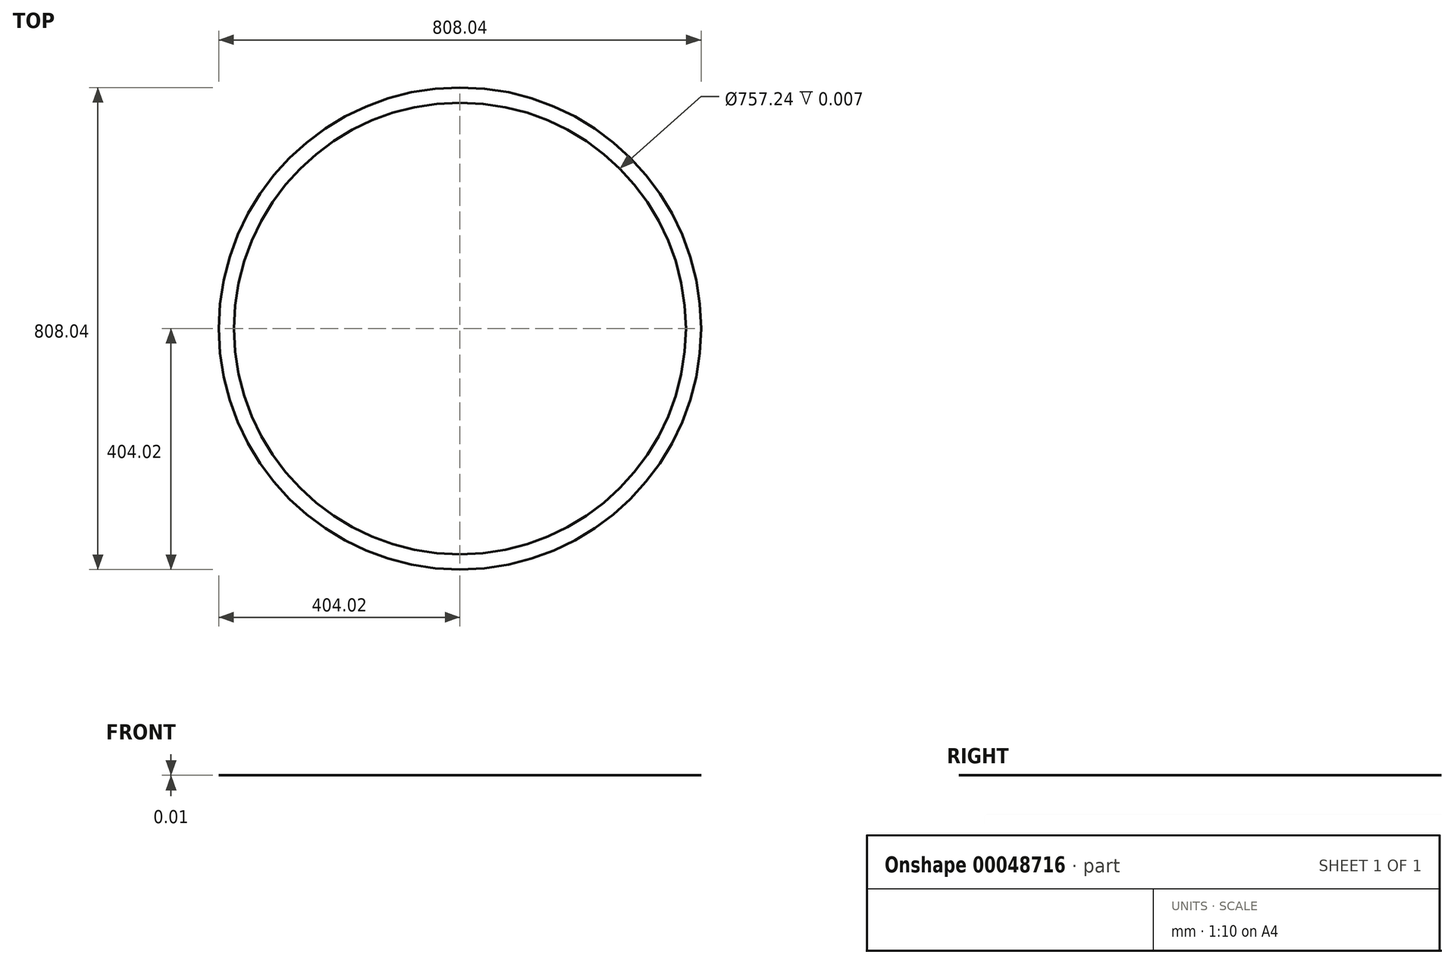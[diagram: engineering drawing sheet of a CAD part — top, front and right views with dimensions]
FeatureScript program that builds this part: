
annotation { "Feature Type Name" : "Feature", "Feature Type Description" : "" }
export const myFeature = defineFeature(function(context is Context, id is Id, definition is map)
    precondition{}
    {
        {
            var Q0;
            Q0=qCreatedBy(makeId("Top.planeOp"),FACE);
            var sketch = newSketch(context, id + "F0", { "sketchPlane" : qUnion([Q0])});
            skCircle(sketch, "E0", {"center": v(0, 0) * mm, "radius": 404.02 * mm});
            skCircle(sketch, "E1", {"center": v(0, 0) * mm, "radius": 378.62 * mm});
            skSolve(sketch);
        }
        {
            var Q0;
            Q0=makeQuery(id+"F0.imprint","IMPRINT",FACE,{"disambiguationData":[TD([[makeQuery(id+"F0.imprint","IMPRINT",EDGE,{"derivedFrom":sQuery(id+"F0.wireOp",EDGE,"E0")}),1.0]])]});
            extrude(context, id + "F1", {"entities" : qUnion([Q0]), "depth" : 3 / 406.4 * mm});
        }
    });
